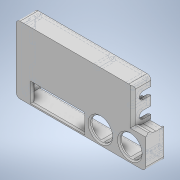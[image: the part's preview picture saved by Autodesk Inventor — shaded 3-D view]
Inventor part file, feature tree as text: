
AUTODESK INVENTOR PART (.ipt)
format: ipt  version: 2021 (Build 250183000, 183)  size: 474,112 bytes
history: native  units: mm
features: sketch x21, extrude x19, fillet x4, chamfer x3, hole x2
ambient origin geometry x8: Origin, YZ Plane, XZ Plane, XY Plane, X Axis, Y Axis, Z Axis, Center Point
bodies: Solid1 (feature_tree)
feature tree (49):
  extrude  "Extrusion1"  Depth=52.0mm
  extrude  "Extrusion2"  Depth=50.0mm
  extrude  "Extrusion3"  Depth=2.0mm
  extrude  "Extrusion4"  Depth=2.0mm
  fillet  "Fillet1"  Radius=2.0mm
  chamfer  "Chamfer1"  Distance=12.0mm
  extrude  "Extrusion5"  Depth=10.4mm
  extrude  "Extrusion6"  Depth=10.4mm
  extrude  "Extrusion7"  Depth=17.0mm
  extrude  "Extrusion8"  Depth=2.0mm
  extrude  "Extrusion9"  Depth=2.0mm
  chamfer  "Chamfer2"  Distance=2.0mm
  fillet  "Fillet2"  Radius=3.0mm
  extrude  "Extrusion10"  Depth=2.0mm
  fillet  "Fillet3"  Radius=29.0mm
  chamfer  "Chamfer3"  Distance=20.0mm
  extrude  "Extrusion11"  Depth=2.0mm TaperAngle=0.0deg
  extrude  "Extrusion12"  Depth=11.0mm
  hole  "Hole1"  [1 undecoded]
  extrude  "Extrusion13"  TaperAngle=0.0deg  [1 undecoded]
  hole  "Hole2"  [1 undecoded]
  extrude  "Extrusion14"  Depth=12.0mm
  extrude  "Extrusion15"  Depth=2.0mm TaperAngle=45.0deg
  extrude  "Extrusion16"  Depth=3.0mm
  extrude  "Extrusion17"  Depth=11.0mm
  extrude  "Extrusion20"  Depth=11.0mm
  fillet  "Fillet4"  Radius=14.0mm
  extrude  "Extrusion21"  Depth=11.0mm
  sketch  "Sketch1"  dims[d0=100.0mm d1=52.0mm]
  sketch  "Sketch2"  dims[d2=26.0mm d3=50.0mm]
  sketch  "Sketch3"  dims[d4=2.0mm d5=0.0mm d6=2.0mm]
  sketch  "Sketch4"  dims[d7=2.0mm d8=2.0mm d9=2.0mm d10=12.0mm d11=0.0mm]
  sketch  "Sketch5"  dims[d12=65.0mm d13=10.4mm]
  sketch  "Sketch6"  dims[d14=87.75mm d15=10.4mm]
  sketch  "Sketch7"  dims[d16=17.0mm d17=17.0mm]
  sketch  "Sketch8"  dims[d18=2.0mm d19=0.0mm d20=40.0mm]
  sketch  "Sketch9"  dims[d21=13.0mm d22=2.0mm]
  sketch  "Sketch10"  dims[d23=12.0mm d24=2.0mm d25=0.0mm d26=3.0mm]
  sketch  "Sketch11"  dims[d27=1.0mm d28=2.0mm d29=45.0deg d30=88.0mm d31=29.0mm]
  sketch  "Sketch12"  dims[d32=23.0mm d33=20.0mm d34=0.0mm]
  sketch  "Sketch13"  dims[d35=2.0mm d36=0.0mm d37=2.0mm d38=0.0mm]
  sketch  "Sketch14"  dims[d39=11.0mm d40=11.0mm]
  sketch  "Sketch15"  dims[d41=42.0mm d42=29.0mm]
  sketch  "Sketch16"  dims[d43=6.0mm d44=0.0mm]
  sketch  "Sketch17"  dims[d45=5.8mm d46=5.8mm]
  sketch  "Sketch18"  dims[d47=2.0mm d48=0.0mm d49=12.0mm]
  sketch  "Sketch19"  dims[d50=20.0mm d51=0.0mm d52=2.0mm d53=2.0mm d54=45.0deg]
  sketch  "Sketch22"  dims[d55=3.0mm d56=30.0mm]
  sketch  "Sketch23"  dims[d57=40.0mm d58=3.5mm d59=6.0mm d60=14.0mm d61=16.0mm d62=2.0mm d63=0.0mm d64=1.0mm d65=1.0mm d66=2.0mm d67=45.0deg d68=3.0mm d69=49.0mm d70=60.0mm d71=49.0mm d72=85.0mm d73=49.0mm d74=2.0mm d75=2.0mm d76=2.0mm d77=5.0mm d78=5.0mm d79=5.0mm d80=12.0mm d81=0.0mm d82=3.0mm d83=3.0mm d84=2.0mm d85=5.0mm d86=12.0mm d87=0.0mm d88=2.0mm d89=6.0mm d90=4.0mm d91=2.0mm d92=90.0deg d93=6.5mm d94=20.594885mm d95=8.0mm d96=97.0mm d97=4.2mm d98=12.0mm d99=0.0mm d100=2.0mm d101=6.0mm d102=4.0mm d103=2.0mm d104=90.0deg d105=6.5mm d106=20.594885mm d107=6.0mm d108=5.8mm d109=5.8mm d110=2.0mm d111=11.0mm d112=0.0mm d113=1.0mm d114=0.0mm d115=2.0mm d116=10.0mm d117=0.0mm d118=0.0mm d119=1.0mm d120=0.0mm d150=17.0mm d151=17.0mm d152=12.0mm d153=0.0mm d160=2.0mm d161=5.0mm d162=1.0mm d163=1.0mm d164=11.0mm d165=0.0mm]
note: 3 required parameter values undecoded (feature->parameter linkage not recoverable at this tier; creation-order binding heuristic only, values carry confidence <= 0.55)
